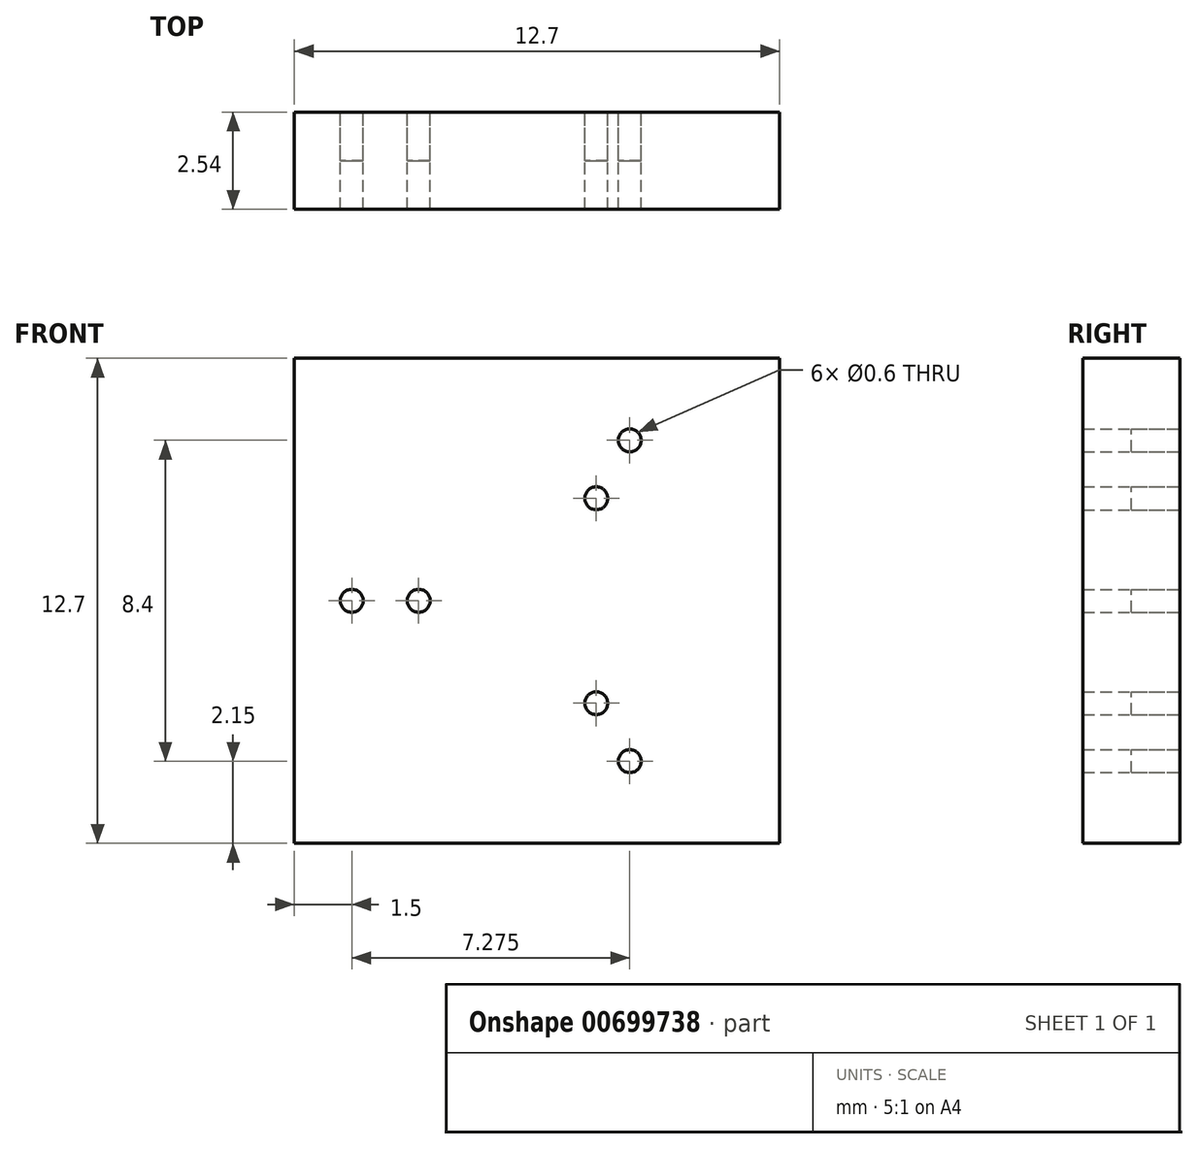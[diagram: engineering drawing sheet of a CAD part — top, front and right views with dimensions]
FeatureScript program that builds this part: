
annotation { "Feature Type Name" : "Feature", "Feature Type Description" : "" }
export const myFeature = defineFeature(function(context is Context, id is Id, definition is map)
    precondition{}
    {
        {
            var Q0;
            Q0=qCreatedBy(makeId("Front.planeOp"),FACE);
            var sketch = newSketch(context, id + "F0", { "sketchPlane" : qUnion([Q0])});
            skCircle(sketch, "E0", {"center": v(0, 0) * mm, "radius": 6.35 * mm});
            skLineSegment(sketch, "E1", {"start": v(-6.35, 6.35) * mm, "end": v(-6.35, -6.35) * mm});
            skLineSegment(sketch, "E2", {"start": v(-6.35, -6.35) * mm, "end": v(6.35, -6.35) * mm});
            skLineSegment(sketch, "E3", {"start": v(6.35, -6.35) * mm, "end": v(6.35, 6.35) * mm});
            skLineSegment(sketch, "E4", {"start": v(6.35, 6.35) * mm, "end": v(-6.35, 6.35) * mm});
            skPoint(sketch, "E5", {"position": v(0, 6.35) * mm});
            skPoint(sketch, "E6", {"position": v(-6.35, 0) * mm});
            skPoint(sketch, "E7", {"position": v(0, -6.35) * mm});
            skPoint(sketch, "E8", {"position": v(6.35, 0) * mm});
            skLineSegment(sketch, "E9", {"start": v(-6.35, 0) * mm, "end": v(0, 0) * mm, "construction": true});
            skCircle(sketch, "E10", {"center": v(-4.85, 0) * mm, "radius": 0.3 * mm});
            skCircle(sketch, "E11", {"center": v(-3.1, 0) * mm, "radius": 0.3 * mm});
            skCircle(sketch, "E12.1.0", {"center": v(1.55, -2.68) * mm, "radius": 0.3 * mm});
            skCircle(sketch, "E12.1.1", {"center": v(2.42, -4.2) * mm, "radius": 0.3 * mm});
            skCircle(sketch, "E12.2.0", {"center": v(1.55, 2.68) * mm, "radius": 0.3 * mm});
            skCircle(sketch, "E12.2.1", {"center": v(2.43, 4.2) * mm, "radius": 0.3 * mm});
            skSolve(sketch);
        }
        {
            var Q0;
            Q0=makeQuery(id+"F0.imprint","IMPRINT",FACE,{"disambiguationData":[TD([[makeQuery(id+"F0.imprint","IMPRINT",EDGE,{"derivedFrom":sQuery(id+"F0.wireOp",EDGE,"E12.2.1")}),1.0]])]});
            var Q1;
            Q1=makeQuery(id+"F0.imprint","IMPRINT",FACE,{"disambiguationData":[TD([[makeQuery(id+"F0.imprint","IMPRINT",EDGE,{"derivedFrom":sQuery(id+"F0.wireOp",EDGE,"E12.2.0")}),1.0]])]});
            var Q2;
            Q2=makeQuery(id+"F0.imprint","IMPRINT",FACE,{"disambiguationData":[TD([[makeQuery(id+"F0.imprint","IMPRINT",EDGE,{"derivedFrom":sQuery(id+"F0.wireOp",EDGE,"E11")}),1.0]])]});
            var Q3;
            Q3=makeQuery(id+"F0.imprint","IMPRINT",FACE,{"disambiguationData":[TD([[makeQuery(id+"F0.imprint","IMPRINT",EDGE,{"derivedFrom":sQuery(id+"F0.wireOp",EDGE,"E10")}),1.0]])]});
            var Q4;
            Q4=makeQuery(id+"F0.imprint","IMPRINT",FACE,{"disambiguationData":[TD([[makeQuery(id+"F0.imprint","IMPRINT",EDGE,{"derivedFrom":sQuery(id+"F0.wireOp",EDGE,"E12.1.0")}),1.0]])]});
            var Q5;
            Q5=makeQuery(id+"F0.imprint","IMPRINT",FACE,{"disambiguationData":[TD([[makeQuery(id+"F0.imprint","IMPRINT",EDGE,{"derivedFrom":sQuery(id+"F0.wireOp",EDGE,"E12.1.1")}),1.0]])]});
            extrude(context, id + "F1", {"entities" : qUnion([Q0, Q1, Q2, Q3, Q4, Q5]), "depth" : 1.27 * mm, "offsetDistance" : 25.4 * mm});
        }
        {
            var Q0;
            Q0 = qSketchRegion(id + "F0", true);
            extrude(context, id + "F2", {"entities" : qUnion([Q0]), "depth" : 2.54 * mm, "offsetDistance" : 25.4 * mm});
        }
    });
